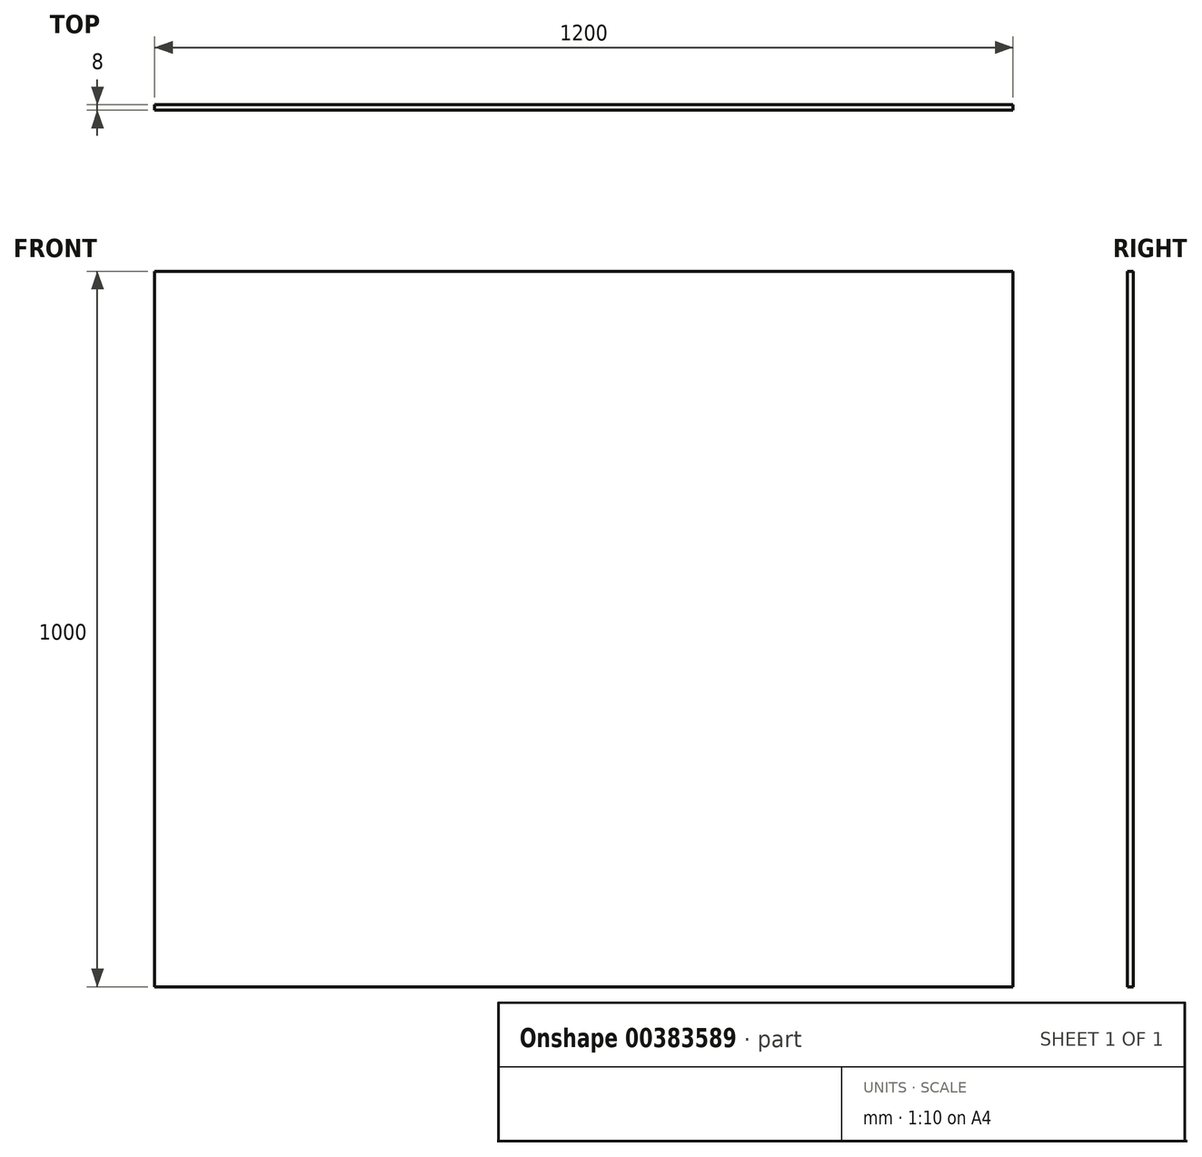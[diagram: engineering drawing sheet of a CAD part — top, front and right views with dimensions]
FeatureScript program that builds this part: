
annotation { "Feature Type Name" : "Feature", "Feature Type Description" : "" }
export const myFeature = defineFeature(function(context is Context, id is Id, definition is map)
    precondition{}
    {
        {
            var Q0;
            Q0=qCreatedBy(makeId("Right.planeOp"),FACE);
            var sketch = newSketch(context, id + "F0", { "sketchPlane" : qUnion([Q0])});
            skLineSegment(sketch, "E0", {"start": v(103.33, -108.3) * mm, "end": v(103.33, -1108.3) * mm});
            skLineSegment(sketch, "E1.0", {"start": v(95.33, -108.3) * mm, "end": v(95.33, -1108.3) * mm});
            skLineSegment(sketch, "E2", {"start": v(95.33, -108.3) * mm, "end": v(103.33, -108.3) * mm});
            skLineSegment(sketch, "E3", {"start": v(95.33, -1108.3) * mm, "end": v(103.33, -1108.3) * mm});
            skSolve(sketch);
        }
        {
            var Q0;
            Q0 = qSketchRegion(id + "F0", true);
            extrude(context, id + "F1", {"entities" : qUnion([Q0]), "depth" : 1200 * mm});
        }
    });
